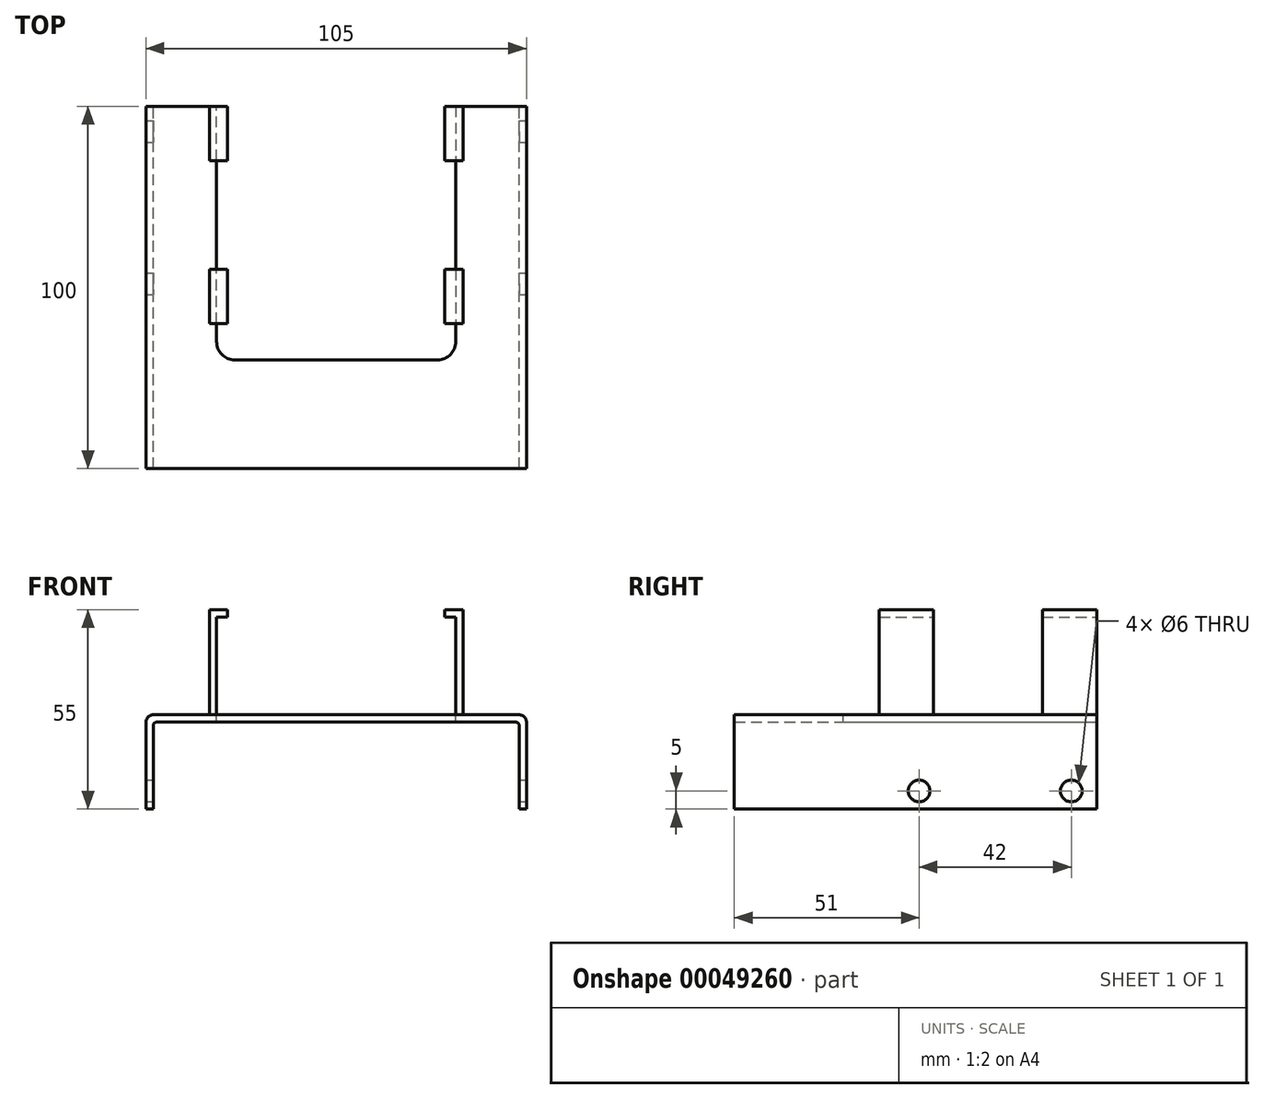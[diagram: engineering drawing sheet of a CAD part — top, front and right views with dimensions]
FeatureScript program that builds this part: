
annotation { "Feature Type Name" : "Feature", "Feature Type Description" : "" }
export const myFeature = defineFeature(function(context is Context, id is Id, definition is map)
    precondition{}
    {
        {
            var Q0;
            Q0=qCreatedBy(makeId("Front.planeOp"),FACE);
            var sketch = newSketch(context, id + "F0", { "sketchPlane" : qUnion([Q0])});
            skLineSegment(sketch, "E0", {"start": v(0, 26) * mm, "end": v(105, 26) * mm});
            skLineSegment(sketch, "E1", {"start": v(103, 0) * mm, "end": v(103, 24) * mm});
            skLineSegment(sketch, "E2", {"start": v(103, 24) * mm, "end": v(2, 24) * mm});
            skLineSegment(sketch, "E3", {"start": v(2, 24) * mm, "end": v(2, 0) * mm});
            skLineSegment(sketch, "E4", {"start": v(103, 0) * mm, "end": v(105, 0) * mm});
            skLineSegment(sketch, "E5", {"start": v(105, 26) * mm, "end": v(105, 0) * mm});
            skLineSegment(sketch, "E6", {"start": v(2, 0) * mm, "end": v(0, 0) * mm});
            skLineSegment(sketch, "E7", {"start": v(0, 26) * mm, "end": v(0, 0) * mm});
            skSolve(sketch);
        }
        {
            var Q0;
            Q0 = qSketchRegion(id + "F0", true);
            extrude(context, id + "F1", {"entities" : qUnion([Q0]), "depth" : 100 * mm});
        }
        {
            var Q0;
            Q0=makeQuery(id+"F1.opExtrude","SWEPT_FACE",FACE,{"disambiguationData":[OSD([sQuery(id+"F0.wireOp",EDGE,"E5")])]});
            var sketch = newSketch(context, id + "F2", { "sketchPlane" : qUnion([Q0])});
            skCircle(sketch, "E8", {"center": v(-7, 5) * mm, "radius": 3 * mm});
            skCircle(sketch, "E9", {"center": v(-49, 5) * mm, "radius": 3 * mm});
            skSolve(sketch);
        }
        {
            var Q0;
            Q0 = qSketchRegion(id + "F2", true);
            extrude(context, id + "F3", {"entities" : qUnion([Q0]), "operationType" : NewBodyOperationType.REMOVE, "endBound" : BoundingType.THROUGH_ALL, "oppositeDirection" : true, "depth" : 25 * mm});
        }
        {
            var Q0;
            Q0=makeQuery(id+"F1.opExtrude","SWEPT_FACE",FACE,{"disambiguationData":[OSD([sQuery(id+"F0.wireOp",EDGE,"E0")])]});
            var sketch = newSketch(context, id + "F4", { "sketchPlane" : qUnion([Q0])});
            skLineSegment(sketch, "E10.bottom", {"start": v(19.5, 0) * mm, "end": v(85.5, 0) * mm});
            skLineSegment(sketch, "E10.top", {"start": v(19.5, -70) * mm, "end": v(85.5, -70) * mm});
            skLineSegment(sketch, "E10.left", {"start": v(19.5, 0) * mm, "end": v(19.5, -70) * mm});
            skLineSegment(sketch, "E10.right", {"start": v(85.5, 0) * mm, "end": v(85.5, -70) * mm});
            skSolve(sketch);
        }
        {
            var Q0;
            Q0 = qSketchRegion(id + "F4", true);
            extrude(context, id + "F5", {"entities" : qUnion([Q0]), "operationType" : NewBodyOperationType.REMOVE, "oppositeDirection" : true, "depth" : 25 * mm});
        }
        {
            var Q0;
            Q0=makeQuery(id+"F1.opExtrude","SWEPT_FACE",FACE,{"disambiguationData":[OSD([sQuery(id+"F0.wireOp",EDGE,"E0")])]});
            var sketch = newSketch(context, id + "F6", { "sketchPlane" : qUnion([Q0])});
            skLineSegment(sketch, "E11.bottom", {"start": v(19.5, 0) * mm, "end": v(17.5, 0) * mm});
            skLineSegment(sketch, "E11.top", {"start": v(19.5, -15) * mm, "end": v(17.5, -15) * mm});
            skLineSegment(sketch, "E11.left", {"start": v(19.5, 0) * mm, "end": v(19.5, -15) * mm});
            skLineSegment(sketch, "E11.right", {"start": v(17.5, 0) * mm, "end": v(17.5, -15) * mm});
            skLineSegment(sketch, "E12.bottom", {"start": v(19.5, -45) * mm, "end": v(17.5, -45) * mm});
            skLineSegment(sketch, "E12.top", {"start": v(19.5, -60) * mm, "end": v(17.5, -60) * mm});
            skLineSegment(sketch, "E12.left", {"start": v(19.5, -45) * mm, "end": v(19.5, -60) * mm});
            skLineSegment(sketch, "E12.right", {"start": v(17.5, -45) * mm, "end": v(17.5, -60) * mm});
            skLineSegment(sketch, "E13.bottom", {"start": v(85.5, 0) * mm, "end": v(87.5, 0) * mm});
            skLineSegment(sketch, "E13.top", {"start": v(85.5, -15) * mm, "end": v(87.5, -15) * mm});
            skLineSegment(sketch, "E13.left", {"start": v(85.5, 0) * mm, "end": v(85.5, -15) * mm});
            skLineSegment(sketch, "E13.right", {"start": v(87.5, 0) * mm, "end": v(87.5, -15) * mm});
            skPoint(sketch, "E14.firstSnap0", {"position": v(85.5, -35) * mm});
            skLineSegment(sketch, "E14.bottom", {"start": v(85.5, -45) * mm, "end": v(87.5, -45) * mm});
            skLineSegment(sketch, "E14.top", {"start": v(85.5, -60) * mm, "end": v(87.5, -60) * mm});
            skLineSegment(sketch, "E14.left", {"start": v(85.5, -45) * mm, "end": v(85.5, -60) * mm});
            skLineSegment(sketch, "E14.right", {"start": v(87.5, -45) * mm, "end": v(87.5, -60) * mm});
            skSolve(sketch);
        }
        {
            var Q0;
            Q0 = qSketchRegion(id + "F6", true);
            extrude(context, id + "F7", {"entities" : qUnion([Q0]), "operationType" : NewBodyOperationType.ADD, "depth" : 29 * mm});
        }
        {
            var Q0;
            Q0=makeQuery(id+"F7.boolean.opBoolean","MERGE",FACE,{"derivedFrom":[makeQuery(id+"F5.boolean.opBoolean","COPY",FACE,{"derivedFrom":makeQuery(id+"F5.opExtrude","SWEPT_FACE",FACE,{"disambiguationData":[OSD([sQuery(id+"F4.wireOp",EDGE,"E10.left")])]})}),makeQuery(id+"F7.opExtrude","SWEPT_FACE",FACE,{"disambiguationData":[OSD([sQuery(id+"F6.wireOp",EDGE,"E11.left")])]}),makeQuery(id+"F7.opExtrude","SWEPT_FACE",FACE,{"disambiguationData":[OSD([sQuery(id+"F6.wireOp",EDGE,"E12.left")])]})]});
            var sketch = newSketch(context, id + "F8", { "sketchPlane" : qUnion([Q0])});
            skLineSegment(sketch, "E15.bottom", {"start": v(-60, 55) * mm, "end": v(-45, 55) * mm});
            skLineSegment(sketch, "E15.top", {"start": v(-60, 53) * mm, "end": v(-45, 53) * mm});
            skLineSegment(sketch, "E15.left", {"start": v(-60, 55) * mm, "end": v(-60, 53) * mm});
            skLineSegment(sketch, "E15.right", {"start": v(-45, 55) * mm, "end": v(-45, 53) * mm});
            skLineSegment(sketch, "E16.bottom", {"start": v(-15, 55) * mm, "end": v(0, 55) * mm});
            skLineSegment(sketch, "E16.top", {"start": v(-15, 53) * mm, "end": v(0, 53) * mm});
            skLineSegment(sketch, "E16.left", {"start": v(-15, 55) * mm, "end": v(-15, 53) * mm});
            skLineSegment(sketch, "E16.right", {"start": v(0, 55) * mm, "end": v(0, 53) * mm});
            skSolve(sketch);
        }
        {
            var Q0;
            Q0 = qSketchRegion(id + "F8", true);
            extrude(context, id + "F9", {"entities" : qUnion([Q0]), "operationType" : NewBodyOperationType.ADD, "depth" : 3 * mm});
        }
        {
            var Q0;
            Q0=makeQuery(id+"F7.boolean.opBoolean","MERGE",FACE,{"derivedFrom":[makeQuery(id+"F5.boolean.opBoolean","COPY",FACE,{"derivedFrom":makeQuery(id+"F5.opExtrude","SWEPT_FACE",FACE,{"disambiguationData":[OSD([sQuery(id+"F4.wireOp",EDGE,"E10.right")])]})}),makeQuery(id+"F7.opExtrude","SWEPT_FACE",FACE,{"disambiguationData":[OSD([sQuery(id+"F6.wireOp",EDGE,"E13.left")])]}),makeQuery(id+"F7.opExtrude","SWEPT_FACE",FACE,{"disambiguationData":[OSD([sQuery(id+"F6.wireOp",EDGE,"E14.left")])]})]});
            var sketch = newSketch(context, id + "F10", { "sketchPlane" : qUnion([Q0])});
            skLineSegment(sketch, "E17.bottom", {"start": v(0, 55) * mm, "end": v(15, 55) * mm});
            skLineSegment(sketch, "E17.top", {"start": v(0, 53) * mm, "end": v(15, 53) * mm});
            skLineSegment(sketch, "E17.left", {"start": v(0, 55) * mm, "end": v(0, 53) * mm});
            skLineSegment(sketch, "E17.right", {"start": v(15, 55) * mm, "end": v(15, 53) * mm});
            skLineSegment(sketch, "E18.bottom", {"start": v(45, 55) * mm, "end": v(60, 55) * mm});
            skLineSegment(sketch, "E18.top", {"start": v(45, 53) * mm, "end": v(60, 53) * mm});
            skLineSegment(sketch, "E18.left", {"start": v(45, 55) * mm, "end": v(45, 53) * mm});
            skLineSegment(sketch, "E18.right", {"start": v(60, 55) * mm, "end": v(60, 53) * mm});
            skSolve(sketch);
        }
        {
            var Q0;
            Q0 = qSketchRegion(id + "F10", true);
            extrude(context, id + "F11", {"entities" : qUnion([Q0]), "operationType" : NewBodyOperationType.ADD, "depth" : 3 * mm});
        }
        {
            var Q0;
            Q0=makeQuery(id+"F1.opExtrude","SWEPT_EDGE",EDGE,{"disambiguationData":[OSD([sQuery(id+"F0.wireOp",EDGE,"E2"),sQuery(id+"F0.wireOp",EDGE,"E3")])]});
            var Q1;
            Q1=makeQuery(id+"F1.opExtrude","SWEPT_EDGE",EDGE,{"disambiguationData":[OSD([sQuery(id+"F0.wireOp",EDGE,"E1"),sQuery(id+"F0.wireOp",EDGE,"E2")])]});
            var Q2;
            Q2=makeQuery(id+"F7.opExtrude","CAP_EDGE",EDGE,{"disambiguationData":[OSD([sQuery(id+"F6.wireOp",EDGE,"E11.right")])],"isStart":true});
            var Q3;
            Q3=makeQuery(id+"F7.opExtrude","CAP_EDGE",EDGE,{"disambiguationData":[OSD([sQuery(id+"F6.wireOp",EDGE,"E11.top")])],"isStart":true});
            var Q4;
            Q4=makeQuery(id+"F7.opExtrude","CAP_EDGE",EDGE,{"disambiguationData":[OSD([sQuery(id+"F6.wireOp",EDGE,"E12.right")])],"isStart":true});
            var Q5;
            Q5=makeQuery(id+"F7.opExtrude","CAP_EDGE",EDGE,{"disambiguationData":[OSD([sQuery(id+"F6.wireOp",EDGE,"E12.top")])],"isStart":true});
            var Q6;
            Q6=makeQuery(id+"F7.opExtrude","CAP_EDGE",EDGE,{"disambiguationData":[OSD([sQuery(id+"F6.wireOp",EDGE,"E12.bottom")])],"isStart":true});
            var Q7;
            Q7=makeQuery(id+"F7.opExtrude","CAP_EDGE",EDGE,{"disambiguationData":[OSD([sQuery(id+"F6.wireOp",EDGE,"E14.top")])],"isStart":true});
            var Q8;
            Q8=makeQuery(id+"F7.opExtrude","CAP_EDGE",EDGE,{"disambiguationData":[OSD([sQuery(id+"F6.wireOp",EDGE,"E14.right")])],"isStart":true});
            var Q9;
            Q9=makeQuery(id+"F7.opExtrude","CAP_EDGE",EDGE,{"disambiguationData":[OSD([sQuery(id+"F6.wireOp",EDGE,"E13.top")])],"isStart":true});
            var Q10;
            Q10=makeQuery(id+"F7.opExtrude","CAP_EDGE",EDGE,{"disambiguationData":[OSD([sQuery(id+"F6.wireOp",EDGE,"E13.right")])],"isStart":true});
            var Q11;
            Q11=makeQuery(id+"F7.opExtrude","CAP_EDGE",EDGE,{"disambiguationData":[OSD([sQuery(id+"F6.wireOp",EDGE,"E14.bottom")])],"isStart":true});
            fillet(context, id + "F12", {"entities" : qUnion([Q0, Q1, Q2, Q3, Q4, Q5, Q6, Q7, Q8, Q9, Q10, Q11]), "radius" : 1 * mm, "tangentPropagation" : true, "allowEdgeOverflow" : false});
        }
        {
            var Q0;
            Q0=makeQuery(id+"F1.opExtrude","SWEPT_EDGE",EDGE,{"disambiguationData":[OSD([sQuery(id+"F0.wireOp",EDGE,"E0"),sQuery(id+"F0.wireOp",EDGE,"E7")])]});
            var Q1;
            Q1=makeQuery(id+"F1.opExtrude","SWEPT_EDGE",EDGE,{"disambiguationData":[OSD([sQuery(id+"F0.wireOp",EDGE,"E0"),sQuery(id+"F0.wireOp",EDGE,"E5")])]});
            fillet(context, id + "F13", {"entities" : qUnion([Q0, Q1]), "radius" : 2 * mm, "tangentPropagation" : true, "allowEdgeOverflow" : false});
        }
        {
            var Q0;
            Q0=makeQuery(id+"F5.boolean.opBoolean","COPY",EDGE,{"derivedFrom":makeQuery(id+"F5.opExtrude","SWEPT_EDGE",EDGE,{"disambiguationData":[OSD([sQuery(id+"F4.wireOp",EDGE,"E10.top"),sQuery(id+"F4.wireOp",EDGE,"E10.right")])]})});
            var Q1;
            Q1=makeQuery(id+"F5.boolean.opBoolean","COPY",EDGE,{"derivedFrom":makeQuery(id+"F5.opExtrude","SWEPT_EDGE",EDGE,{"disambiguationData":[OSD([sQuery(id+"F4.wireOp",EDGE,"E10.top"),sQuery(id+"F4.wireOp",EDGE,"E10.left")])]})});
            fillet(context, id + "F14", {"entities" : qUnion([Q0, Q1]), "radius" : 5 * mm, "tangentPropagation" : true, "allowEdgeOverflow" : false});
        }
    });
